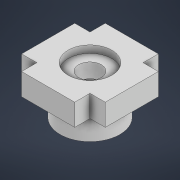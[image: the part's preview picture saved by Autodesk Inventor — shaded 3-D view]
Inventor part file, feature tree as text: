
AUTODESK INVENTOR PART (.ipt)
format: ipt  version: 2021 (Build 250183000, 183)  size: 308,736 bytes
history: native  units: mm
features: extrude x5, sketch x4, other x1, plane x1
ambient origin geometry x8: Origin, YZ Plane, XZ Plane, XY Plane, X Axis, Y Axis, Z Axis, Center Point
bodies: Volumenkörper1 (feature_tree)
feature tree (11):
  other  "Zahnrad_innen"
  extrude  "Extrusion1"  Depth=11.5mm
  sketch  "Skizze2"  dims[d3=11.5mm d12=3.0mm d13=0.0mm]
  plane  "Arbeitsebene1"
  extrude  "Extrusion4"  Depth=3.0mm TaperAngle=0.0deg
  extrude  "Extrusion5"  Depth=6.0mm
  extrude  "Extrusion6"  Depth=3.5mm TaperAngle=0.0deg
  extrude  "Extrusion7"  Depth=2.1mm
  sketch  "Skizze1"  dims[d1=7.0mm d2=11.5mm]
  sketch  "Skizze5"  dims[d14=6.0mm d20=6.0mm]
  sketch  "Skizze6"  dims[d21=8.2mm d22=3.5mm d23=0.0mm d24=2.1mm d25=2.1mm d26=2.1mm d27=2.1mm d28=2.1mm d29=2.1mm d30=2.1mm d31=2.1mm d32=6.0mm d33=0.0mm d34=1.0mm d35=0.0mm d38=3.1mm d39=10.0mm d40=0.0mm d15=0.5mm d16=0.872665mm d17=0.5mm d18=0.872665mm d36=0.5mm d37=0.872665mm]
